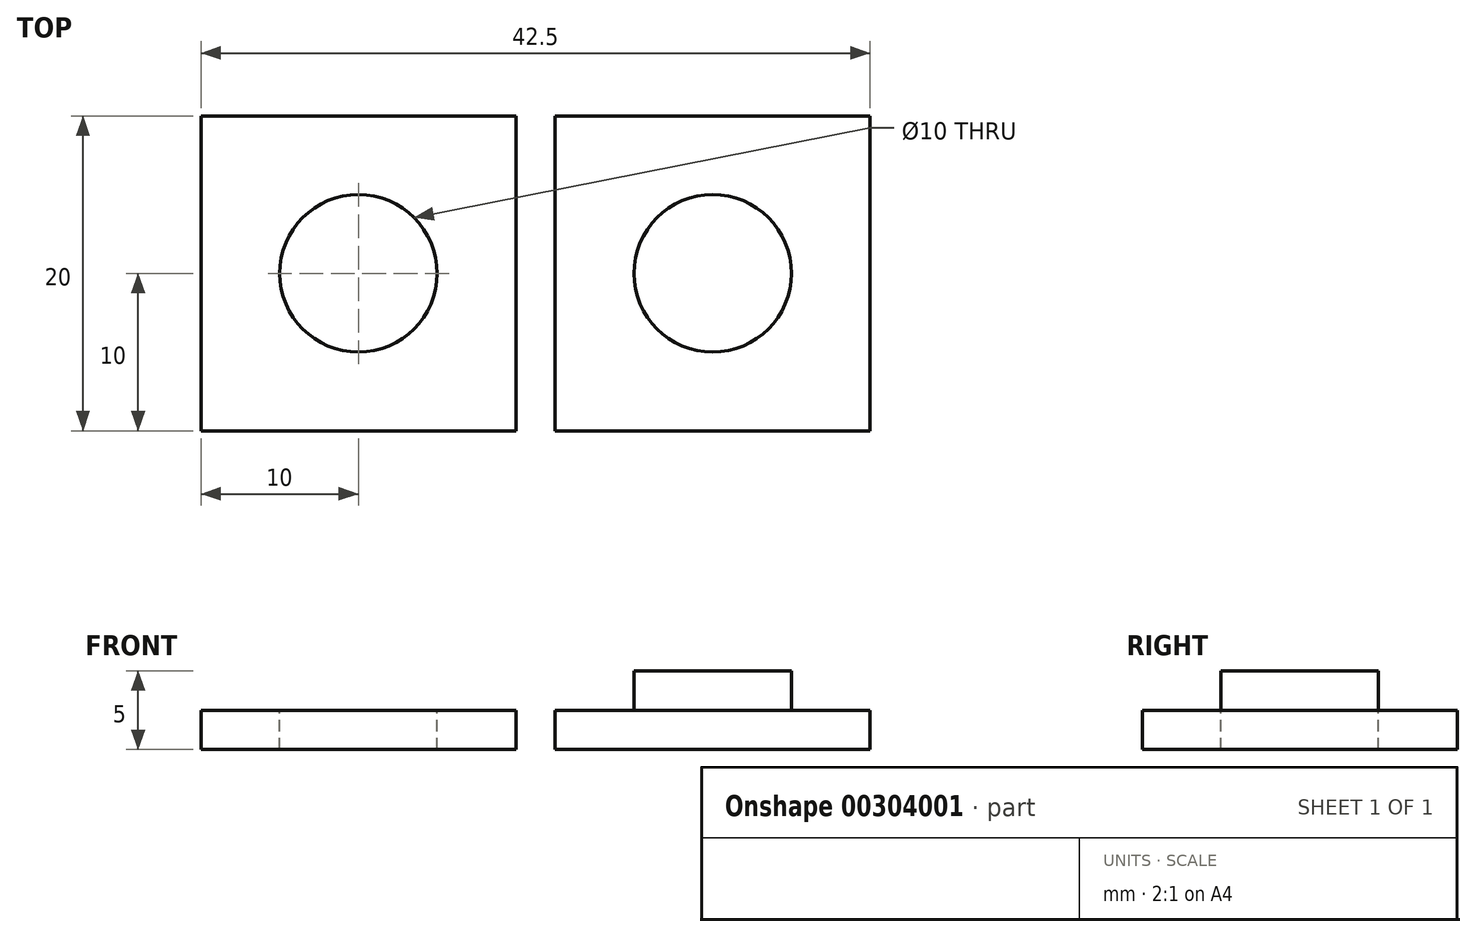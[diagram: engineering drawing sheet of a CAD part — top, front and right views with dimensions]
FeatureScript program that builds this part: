
annotation { "Feature Type Name" : "Feature", "Feature Type Description" : "" }
export const myFeature = defineFeature(function(context is Context, id is Id, definition is map)
    precondition{}
    {
        {
            var Q0;
            Q0=qCreatedBy(makeId("Top.planeOp"),FACE);
            var sketch = newSketch(context, id + "F0", { "sketchPlane" : qUnion([Q0])});
            skLineSegment(sketch, "E0.bottom", {"start": v(10, -10) * mm, "end": v(-10, -10) * mm});
            skLineSegment(sketch, "E0.top", {"start": v(10, 10) * mm, "end": v(-10, 10) * mm});
            skLineSegment(sketch, "E0.left", {"start": v(10, -10) * mm, "end": v(10, 10) * mm});
            skLineSegment(sketch, "E0.right", {"start": v(-10, -10) * mm, "end": v(-10, 10) * mm});
            skPoint(sketch, "E0.middle", {"position": v(0, 0) * mm});
            skCircle(sketch, "E1", {"center": v(0, 0) * mm, "radius": 5 * mm});
            skSolve(sketch);
        }
        {
            var Q0;
            Q0=makeQuery(id+"F0.imprint","IMPRINT",FACE,{"disambiguationData":[TD([[makeQuery(id+"F0.imprint","IMPRINT",EDGE,{"derivedFrom":sQuery(id+"F0.wireOp",EDGE,"E0.bottom")}),-1.0]])]});
            extrude(context, id + "F1", {"entities" : qUnion([Q0]), "oppositeDirection" : true, "depth" : 2.5 * mm});
        }
        {
            var Q0;
            Q0=makeQuery(id+"F0.imprint","IMPRINT",FACE,{"disambiguationData":[TD([[makeQuery(id+"F0.imprint","IMPRINT",EDGE,{"derivedFrom":sQuery(id+"F0.wireOp",EDGE,"E1")}),1.0]])]});
            extrude(context, id + "F2", {"entities" : qUnion([Q0]), "operationType" : NewBodyOperationType.ADD, "endBound" : BoundingType.SYMMETRIC, "depth" : 5 * mm});
        }
        {
            var Q0;
            Q0=makeQuery(id+"F0.imprint","IMPRINT",FACE,{"disambiguationData":[TD([[makeQuery(id+"F0.imprint","IMPRINT",EDGE,{"derivedFrom":sQuery(id+"F0.wireOp",EDGE,"E0.bottom")}),-1.0]])]});
            extrude(context, id + "F3", {"entities" : qUnion([Q0]), "depth" : 2.5 * mm});
        }
        {
            var Q0;
            Q0=makeQuery(id+"F3.opExtrude","SWEPT_BODY",BODY,{"disambiguationData":[OSD([sQuery(id+"F0.wireOp",EDGE,"E0.bottom"),sQuery(id+"F0.wireOp",EDGE,"E0.top"),sQuery(id+"F0.wireOp",EDGE,"E0.left"),sQuery(id+"F0.wireOp",EDGE,"E0.right"),sQuery(id+"F0.wireOp",EDGE,"E1")])]});
            var Q1;
            Q1=sQuery(id+"F0.wireOp",EDGE,"E0.right");
            transform(context, id + "F4", {"entities" : qUnion([Q0]), "transformType" : TransformType.ROTATION, "transformAxis" : qUnion([Q1]), "angle" : 180 * degree, "makeCopy" : false});
        }
        {
            var Q0;
            Q0=makeQuery(id+"F1.opExtrude","SWEPT_BODY",BODY,{"disambiguationData":[OSD([sQuery(id+"F0.wireOp",EDGE,"E0.bottom"),sQuery(id+"F0.wireOp",EDGE,"E0.top"),sQuery(id+"F0.wireOp",EDGE,"E0.left"),sQuery(id+"F0.wireOp",EDGE,"E0.right"),sQuery(id+"F0.wireOp",EDGE,"E1")])]});
            transform(context, id + "F5", {"entities" : qUnion([Q0]), "transformType" : TransformType.TRANSLATION_3D, "dx" : 2.5 * mm, "dy" : 0 * mm, "dz" : 0 * mm, "makeCopy" : false});
        }
    });
